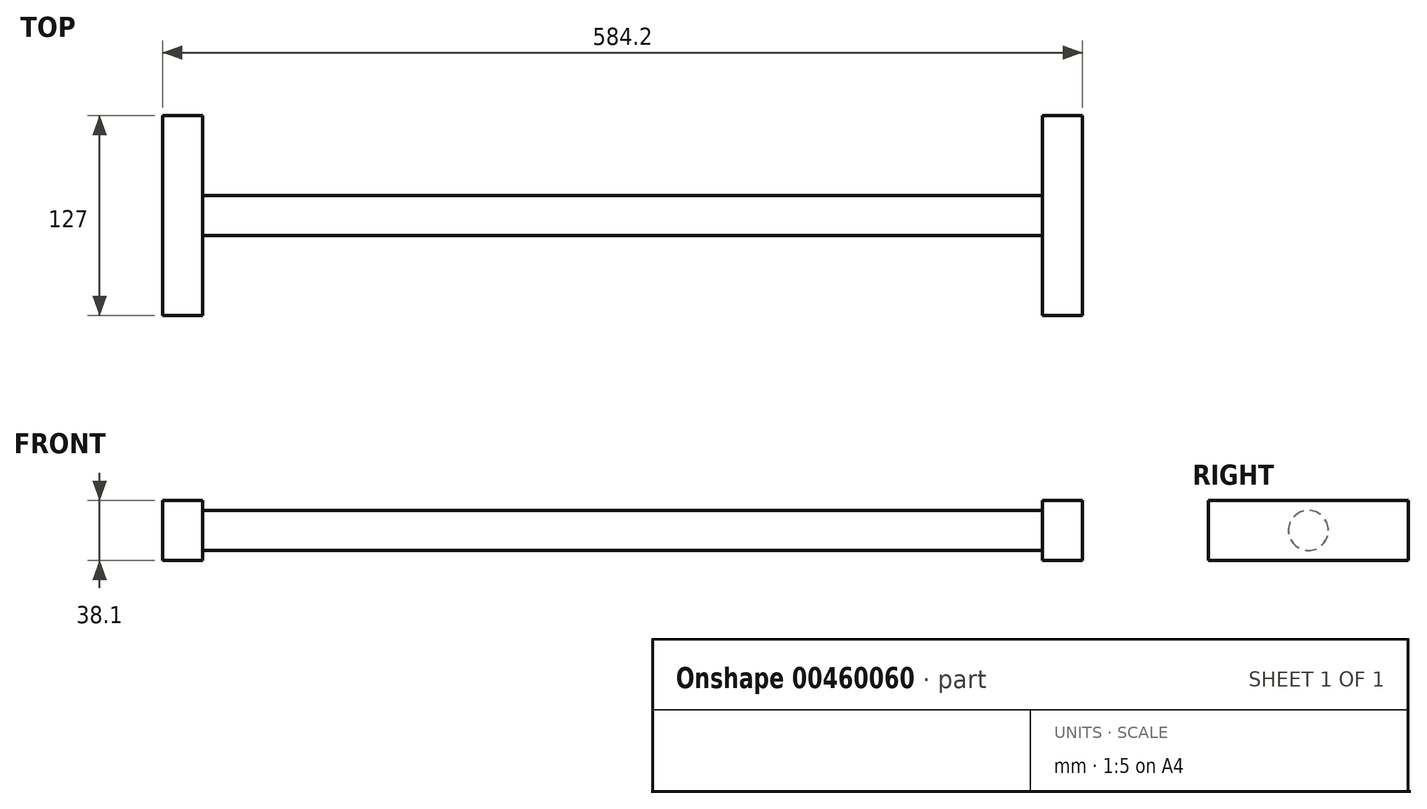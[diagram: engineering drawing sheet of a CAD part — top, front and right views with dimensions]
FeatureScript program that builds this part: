
annotation { "Feature Type Name" : "Feature", "Feature Type Description" : "" }
export const myFeature = defineFeature(function(context is Context, id is Id, definition is map)
    precondition{}
    {
        {
            var Q0;
            Q0=qCreatedBy(makeId("Top.planeOp"),FACE);
            var sketch = newSketch(context, id + "F0", { "sketchPlane" : qUnion([Q0])});
            skLineSegment(sketch, "E0.bottom", {"start": v(-71.7, 91.77) * mm, "end": v(-46.3, 91.77) * mm});
            skLineSegment(sketch, "E0.top", {"start": v(-71.7, -35.23) * mm, "end": v(-46.3, -35.23) * mm});
            skLineSegment(sketch, "E0.left", {"start": v(-71.7, 91.77) * mm, "end": v(-71.7, -35.23) * mm});
            skLineSegment(sketch, "E0.right", {"start": v(-46.3, 91.77) * mm, "end": v(-46.3, -35.23) * mm});
            skLineSegment(sketch, "E1.left", {"start": v(-46.3, 40.97) * mm, "end": v(-46.3, 15.57) * mm});
            skSolve(sketch);
        }
        {
            var Q0;
            Q0 = qSketchRegion(id + "F0", true);
            extrude(context, id + "F1", {"entities" : qUnion([Q0]), "depth" : 38.1 * mm});
        }
        {
            var Q0;
            Q0=makeQuery(id+"F1.opExtrude","SWEPT_FACE",FACE,{"disambiguationData":[OSD([sQuery(id+"F0.wireOp",EDGE,"E0.right"),sQuery(id+"F0.wireOp",EDGE,"E1.left")])]});
            var sketch = newSketch(context, id + "F2", { "sketchPlane" : qUnion([Q0])});
            skCircle(sketch, "E2", {"center": v(28.27, 19.05) * mm, "radius": 12.7 * mm});
            skPoint(sketch, "E2.centerSnap0", {"position": v(28.27, 44.45) * mm});
            skPoint(sketch, "E3", {"position": v(28.27, 38.1) * mm});
            skPoint(sketch, "E4", {"position": v(-35.23, 19.05) * mm});
            skSolve(sketch);
        }
        {
            var Q0;
            Q0 = qSketchRegion(id + "F2", true);
            extrude(context, id + "F3", {"entities" : qUnion([Q0]), "operationType" : NewBodyOperationType.ADD, "depth" : 533.4 * mm});
        }
        {
            var Q0;
            Q0=makeQuery(id+"F3.opExtrude","CAP_FACE",FACE,{"disambiguationData":[OSD([sQuery(id+"F2.wireOp",EDGE,"E2")])],"isStart":false});
            var sketch = newSketch(context, id + "F4", { "sketchPlane" : qUnion([Q0])});
            skLineSegment(sketch, "E5.bottom", {"start": v(91.77, 38.1) * mm, "end": v(-35.23, 38.1) * mm});
            skLineSegment(sketch, "E5.top", {"start": v(91.77, 0) * mm, "end": v(-35.23, 0) * mm});
            skLineSegment(sketch, "E5.left", {"start": v(91.77, 38.1) * mm, "end": v(91.77, 0) * mm});
            skLineSegment(sketch, "E5.right", {"start": v(-35.23, 38.1) * mm, "end": v(-35.23, 0) * mm});
            skPoint(sketch, "E5.middle", {"position": v(28.27, 19.05) * mm});
            skSolve(sketch);
        }
        {
            var Q0;
            Q0 = qSketchRegion(id + "F4", true);
            extrude(context, id + "F5", {"entities" : qUnion([Q0]), "operationType" : NewBodyOperationType.ADD, "depth" : 25.4 * mm});
        }
    });
